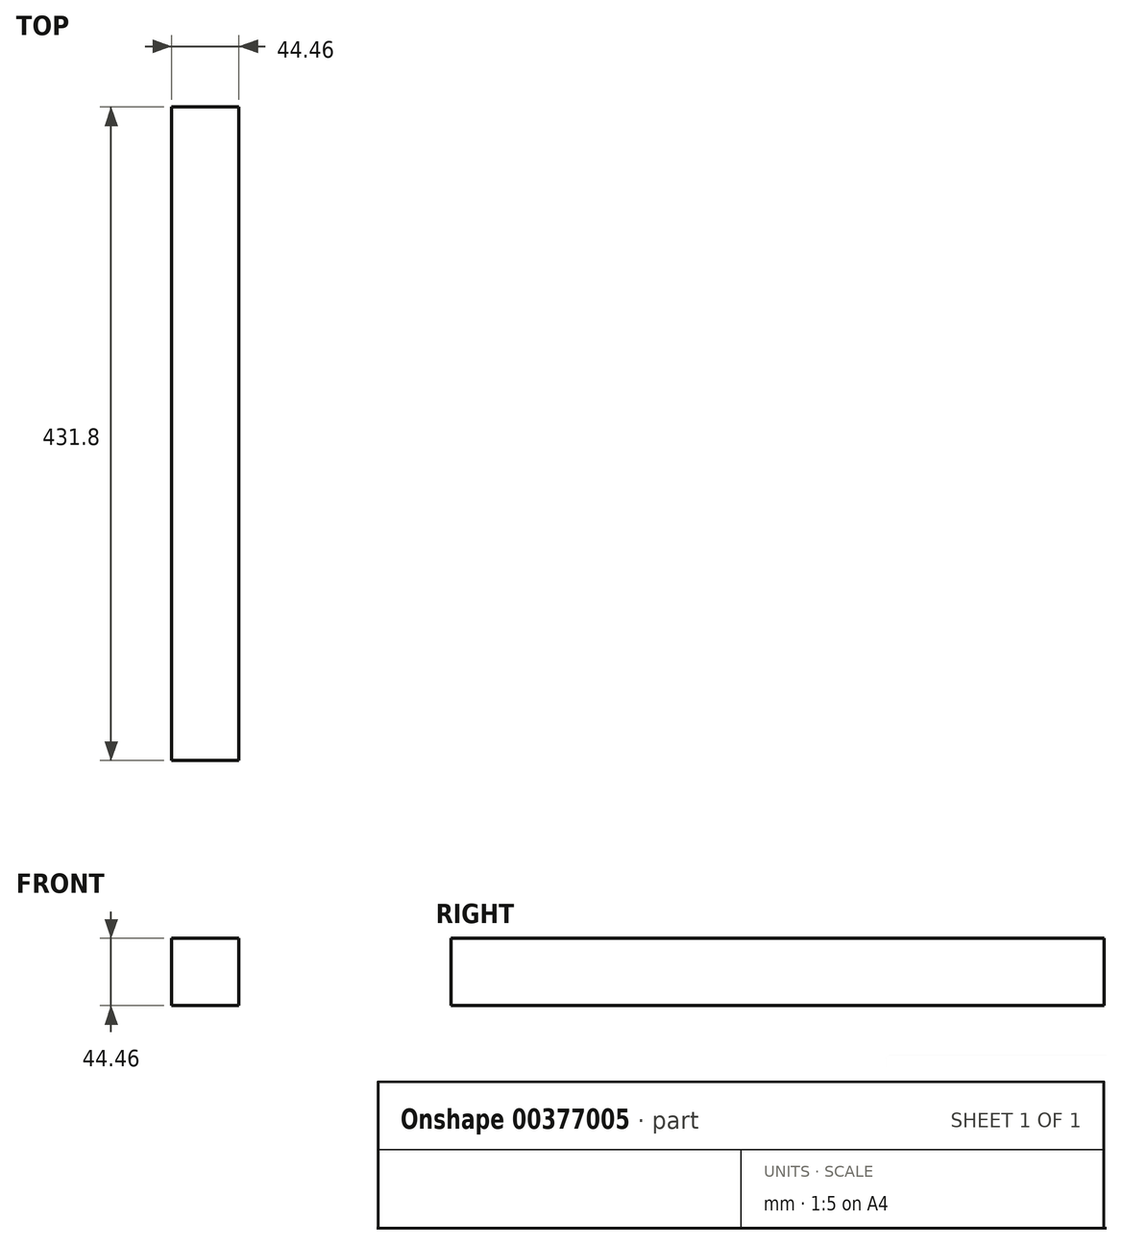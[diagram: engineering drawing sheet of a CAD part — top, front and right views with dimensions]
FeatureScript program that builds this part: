
annotation { "Feature Type Name" : "Feature", "Feature Type Description" : "" }
export const myFeature = defineFeature(function(context is Context, id is Id, definition is map)
    precondition{}
    {
        {
            var Q0;
            Q0=qCreatedBy(makeId("Front.planeOp"),FACE);
            var sketch = newSketch(context, id + "F0", { "sketchPlane" : qUnion([Q0])});
            skLineSegment(sketch, "E0.bottom", {"start": v(22.23, 22.22) * mm, "end": v(-22.23, 22.22) * mm});
            skLineSegment(sketch, "E0.top", {"start": v(22.23, -22.23) * mm, "end": v(-22.23, -22.23) * mm});
            skLineSegment(sketch, "E0.left", {"start": v(22.23, 22.22) * mm, "end": v(22.23, -22.23) * mm});
            skLineSegment(sketch, "E0.right", {"start": v(-22.23, 22.22) * mm, "end": v(-22.23, -22.23) * mm});
            skPoint(sketch, "E0.middle", {"position": v(0, 0) * mm});
            skSolve(sketch);
        }
        {
            var Q0;
            Q0=makeQuery(id+"F0.imprint","IMPRINT",FACE,{"disambiguationData":[TD([[makeQuery(id+"F0.imprint","IMPRINT",EDGE,{"derivedFrom":sQuery(id+"F0.wireOp",EDGE,"E0.bottom")}),1.0]])]});
            extrude(context, id + "F1", {"entities" : qUnion([Q0]), "depth" : 431.8 * mm});
        }
    });
